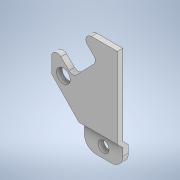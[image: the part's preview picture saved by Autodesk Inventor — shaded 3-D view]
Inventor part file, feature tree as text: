
AUTODESK INVENTOR PART (.ipt)
format: ipt  version: 2020 (Build 240168000, 168)  size: 254,464 bytes
history: native  units: mm
features: extrude x6, sketch x6, fillet x3, chamfer x2, projected_geometry x2
ambient origin geometry x8: Origin, YZ Plane, XZ Plane, XY Plane, X Axis, Y Axis, Z Axis, Center Point
bodies: Solid1 (feature_tree)
feature tree (19):
  extrude  "Extrusion1"  TaperAngle=0.0deg  [1 undecoded]
  extrude  "Extrusion5"  Depth=5.0mm
  fillet  "Fillet2"  Radius=2.5mm
  extrude  "Extrusion6"  Depth=1.0mm
  chamfer  "Chamfer1"  Distance=0.1mm
  extrude  "Extrusion7"  Depth=1.0mm
  chamfer  "Chamfer2"  [1 undecoded]
  extrude  "Extrusion8"  Depth=1.0mm
  extrude  "Extrusion9"  Depth=2.0mm
  fillet  "Fillet3"  Radius=3.525mm
  fillet  "Fillet4"  Radius=2.6mm
  sketch  "Sketch1"  dims[d6=1.0mm d7=0.0mm]
  sketch  "Sketch7"  dims[d26=4.95mm d27=7.25mm d28=2.5mm d29=4.9mm d30=14.9mm d31=5.1mm d32=5.1mm d33=90.0deg d34=135.0deg d36=0.0mm d37=0.0mm]
  projected_geometry  "Projected Loop2"
  sketch  "Sketch8"  dims[d38=2.5mm d39=5.0mm d40=2.5mm]
  sketch  "Sketch9"  dims[d41=1.0mm d42=7.5mm]
  projected_geometry  "Projected Loop3"
  sketch  "Sketch10"  dims[d43=0.15mm]
  sketch  "Sketch11"  dims[d44=0.15mm d54=0.1mm d55=0.1mm d56=0.0mm d57=4.5mm d58=2.0mm d59=3.525mm d60=2.6mm d61=2.0mm d62=0.0mm d63=5.0mm d64=45.0deg d65=5.0mm d66=45.0deg d67=2.1mm d68=0.2mm d69=0.1mm d70=10.0mm d71=0.0mm d72=1.0mm d73=2.0mm d74=45.0deg d75=1.0mm d76=0.0mm d77=1.0mm d78=2.0mm d79=45.0deg d80=3.8mm d81=1.0mm d82=0.0mm d83=7.0mm d85=6.5mm d86=3.5mm d87=1.0mm d88=0.0mm d89=6.5mm d90=1.0mm d91=1.0mm d5=0.5mm d8=0.872665mm d11=0.5mm d12=0.872665mm d13=0.5mm d14=0.872665mm d25=0.5mm]
note: 2 required parameter values undecoded (feature->parameter linkage not recoverable at this tier; creation-order binding heuristic only, values carry confidence <= 0.55)
